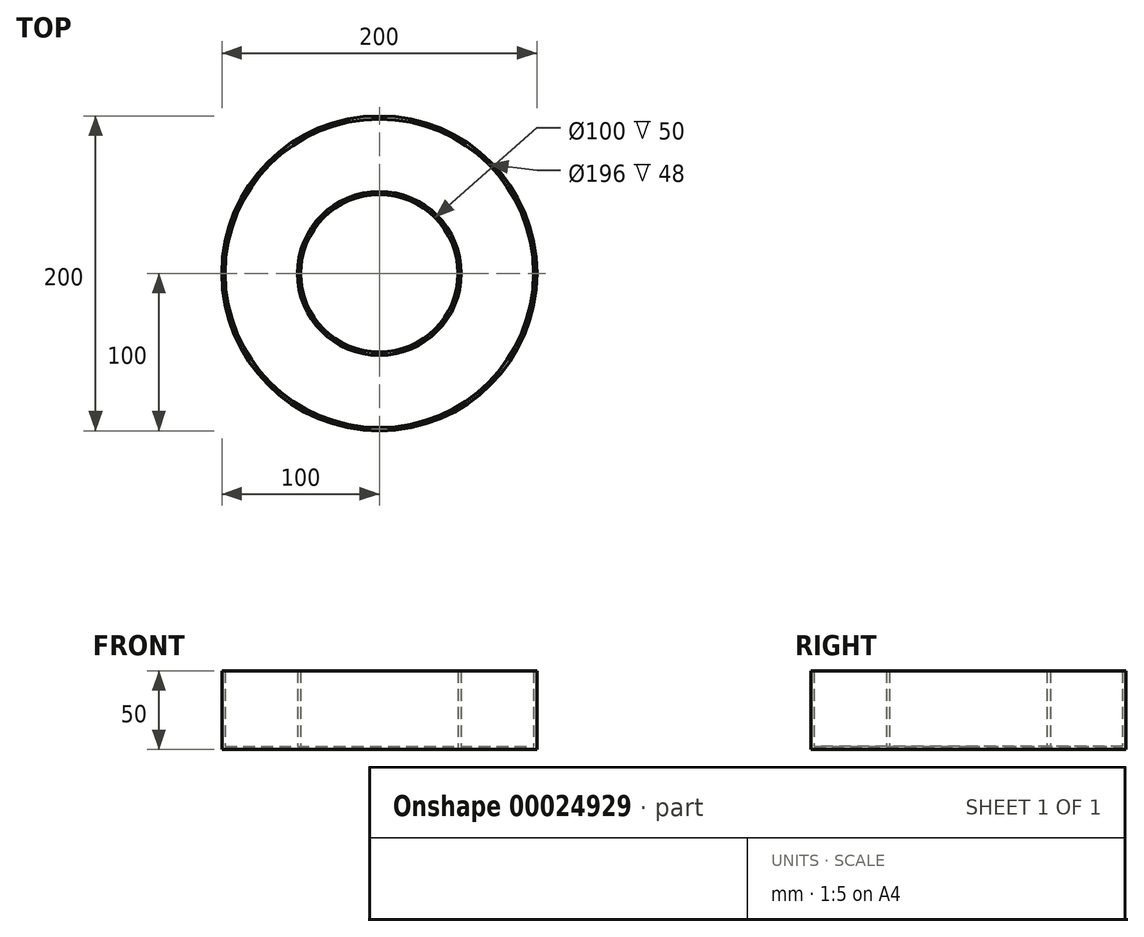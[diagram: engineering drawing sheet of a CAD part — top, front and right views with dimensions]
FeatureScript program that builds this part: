
annotation { "Feature Type Name" : "Feature", "Feature Type Description" : "" }
export const myFeature = defineFeature(function(context is Context, id is Id, definition is map)
    precondition{}
    {
        {
            var Q0;
            Q0=qCreatedBy(makeId("Front.planeOp"),FACE);
            var sketch = newSketch(context, id + "F0", { "sketchPlane" : qUnion([Q0])});
            skLineSegment(sketch, "E0", {"start": v(0, 0) * mm, "end": v(-100, 0) * mm});
            skLineSegment(sketch, "E1", {"start": v(-100, 0) * mm, "end": v(-100, 50) * mm});
            skLineSegment(sketch, "E2", {"start": v(-100, 50) * mm, "end": v(-98, 50) * mm});
            skLineSegment(sketch, "E3", {"start": v(-98, 50) * mm, "end": v(-98, 2) * mm});
            skLineSegment(sketch, "E4", {"start": v(-98, 2) * mm, "end": v(-52, 2) * mm});
            skLineSegment(sketch, "E5", {"start": v(-52, 2) * mm, "end": v(-52, 50) * mm});
            skLineSegment(sketch, "E6", {"start": v(-52, 50) * mm, "end": v(-50, 50) * mm});
            skLineSegment(sketch, "E7", {"start": v(-50, 50) * mm, "end": v(-50, 0) * mm});
            skSolve(sketch);
        }
        {
            var Q0;
            Q0=qCreatedBy(makeId("Right.planeOp"),FACE);
            var sketch = newSketch(context, id + "F1", { "sketchPlane" : qUnion([Q0])});
            skLineSegment(sketch, "E8", {"start": v(0, 0) * mm, "end": v(0, 61.45) * mm});
            skSolve(sketch);
        }
        {
            var Q0;
            Q0 = qSketchRegion(id + "F0", true);
            var Q1;
            Q1=sQuery(id+"F1.wireOp",EDGE,"E8");
            revolve(context, id + "F2", {"entities" : qUnion([Q0]), "axis" : qUnion([Q1]), "revolveType" : RevolveType.FULL});
        }
    });
